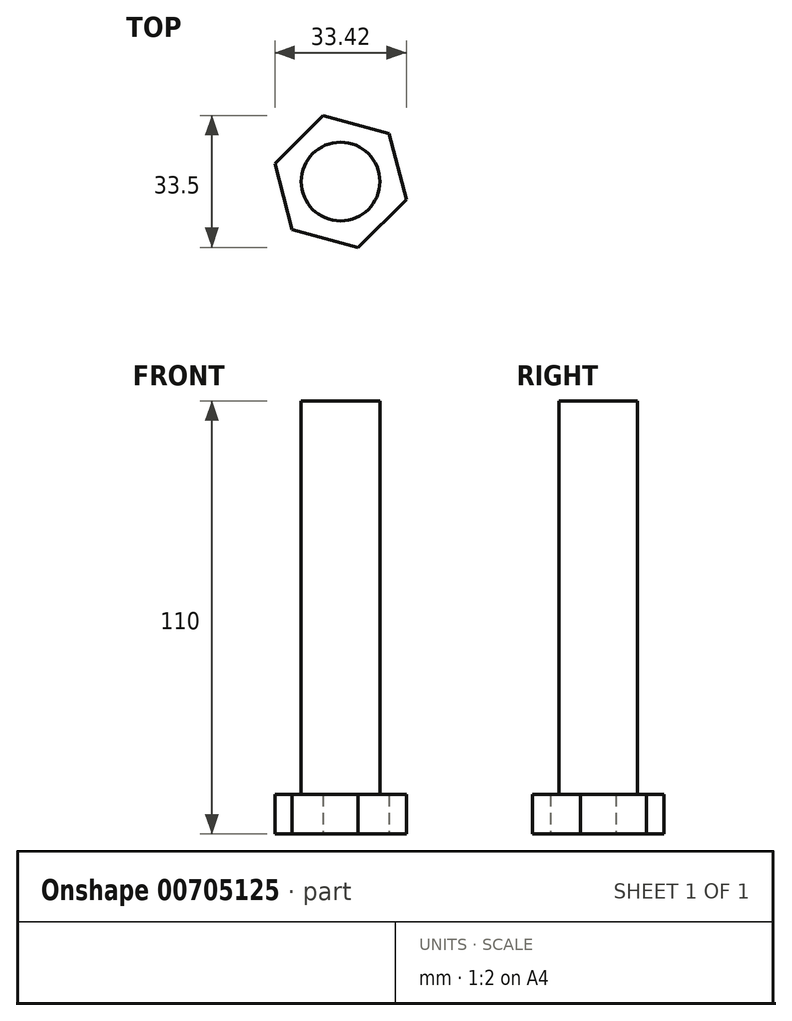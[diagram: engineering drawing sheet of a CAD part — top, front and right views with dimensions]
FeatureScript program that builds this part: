
annotation { "Feature Type Name" : "Feature", "Feature Type Description" : "" }
export const myFeature = defineFeature(function(context is Context, id is Id, definition is map)
    precondition{}
    {
        {
            var Q0;
            Q0=qCreatedBy(makeId("Top.planeOp"),FACE);
            var sketch = newSketch(context, id + "F0", { "sketchPlane" : qUnion([Q0])});
            skCircle(sketch, "E0", {"center": v(0, 0) * mm, "radius": 10 * mm});
            skSolve(sketch);
        }
        {
            var Q0;
            Q0=makeQuery(id+"F0.imprint","IMPRINT",FACE,{"disambiguationData":[TD([[makeQuery(id+"F0.imprint","IMPRINT",EDGE,{"derivedFrom":sQuery(id+"F0.wireOp",EDGE,"E0")}),1.0]])]});
            extrude(context, id + "F1", {"entities" : qUnion([Q0]), "depth" : 110 * mm, "offsetDistance" : 25 * mm});
        }
        {
            var Q0;
            Q0=makeQuery(id+"F1.opExtrude","CAP_FACE",FACE,{"disambiguationData":[OSD([sQuery(id+"F0.wireOp",EDGE,"E0")])],"isStart":true});
            var sketch = newSketch(context, id + "F2", { "sketchPlane" : qUnion([Q0])});
            skCircle(sketch, "E1.cCircle", {"center": v(0, 0) * mm, "radius": 15 * mm, "construction": true});
            skLineSegment(sketch, "E1.0", {"start": v(16.71, 4.55) * mm, "end": v(12.3, -12.2) * mm});
            skLineSegment(sketch, "E1.1", {"start": v(12.3, -12.2) * mm, "end": v(-4.42, -16.75) * mm});
            skLineSegment(sketch, "E1.2", {"start": v(-4.42, -16.75) * mm, "end": v(-16.71, -4.55) * mm});
            skLineSegment(sketch, "E1.3", {"start": v(-16.71, -4.55) * mm, "end": v(-12.3, 12.2) * mm});
            skLineSegment(sketch, "E1.4", {"start": v(-12.3, 12.2) * mm, "end": v(4.42, 16.75) * mm});
            skLineSegment(sketch, "E1.5", {"start": v(4.42, 16.75) * mm, "end": v(16.71, 4.55) * mm});
            skPoint(sketch, "E1.0.midPoint", {"position": v(14.5, -3.82) * mm});
            skSolve(sketch);
        }
        {
            var Q0;
            Q0=makeQuery(id+"F2.imprint","IMPRINT",FACE,{"disambiguationData":[TD([[makeQuery(id+"F2.imprint","IMPRINT",EDGE,{"derivedFrom":sQuery(id+"F2.wireOp",EDGE,"E1.0")}),-1.0]])]});
            var Q1;
            Q1=makeQuery(id+"F2.imprint","IMPRINT",FACE,{"disambiguationData":[TD([[makeQuery(id+"F2.imprint","IMPRINT",EDGE,{"derivedFrom":makeQuery(id+"F1.opExtrude","CAP_EDGE",EDGE,{"disambiguationData":[OSD([sQuery(id+"F0.wireOp",EDGE,"E0")])],"isStart":true})}),-1.0]])]});
            extrude(context, id + "F3", {"entities" : qUnion([Q0, Q1]), "operationType" : NewBodyOperationType.ADD, "oppositeDirection" : true, "depth" : 10 * mm, "offsetDistance" : 25 * mm});
        }
    });
